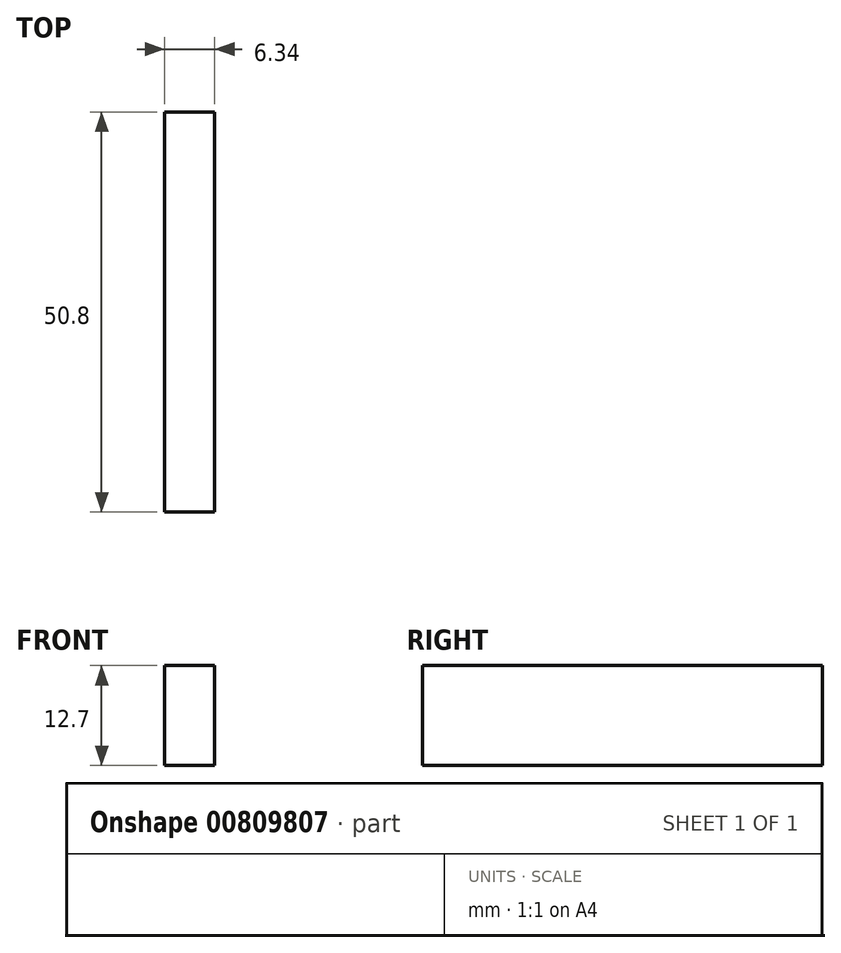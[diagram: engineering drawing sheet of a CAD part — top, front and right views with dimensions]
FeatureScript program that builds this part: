
annotation { "Feature Type Name" : "Feature", "Feature Type Description" : "" }
export const myFeature = defineFeature(function(context is Context, id is Id, definition is map)
    precondition{}
    {
        {
            var Q0;
            Q0=qCreatedBy(makeId("Top.planeOp"),FACE);
            var sketch = newSketch(context, id + "F0", { "sketchPlane" : qUnion([Q0])});
            skLineSegment(sketch, "E0", {"start": v(-3.17, 18.78) * mm, "end": v(-3.18, 69.58) * mm});
            skLineSegment(sketch, "E1", {"start": v(-3.18, 69.58) * mm, "end": v(3.18, 69.58) * mm});
            skLineSegment(sketch, "E2", {"start": v(3.17, 69.58) * mm, "end": v(3.18, 18.78) * mm});
            skLineSegment(sketch, "E3", {"start": v(-3.18, 69.58) * mm, "end": v(0, 69.58) * mm});
            skLineSegment(sketch, "E4", {"start": v(-3.17, 18.78) * mm, "end": v(3.17, 18.78) * mm});
            skSolve(sketch);
        }
        {
            var Q0;
            Q0=qSketchRegion(id+"F0",true);
            extrude(context, id + "F1", {"entities" : qUnion([Q0]), "depth" : 12.7 * mm, "offsetDistance" : 25.4 * mm});
        }
    });
